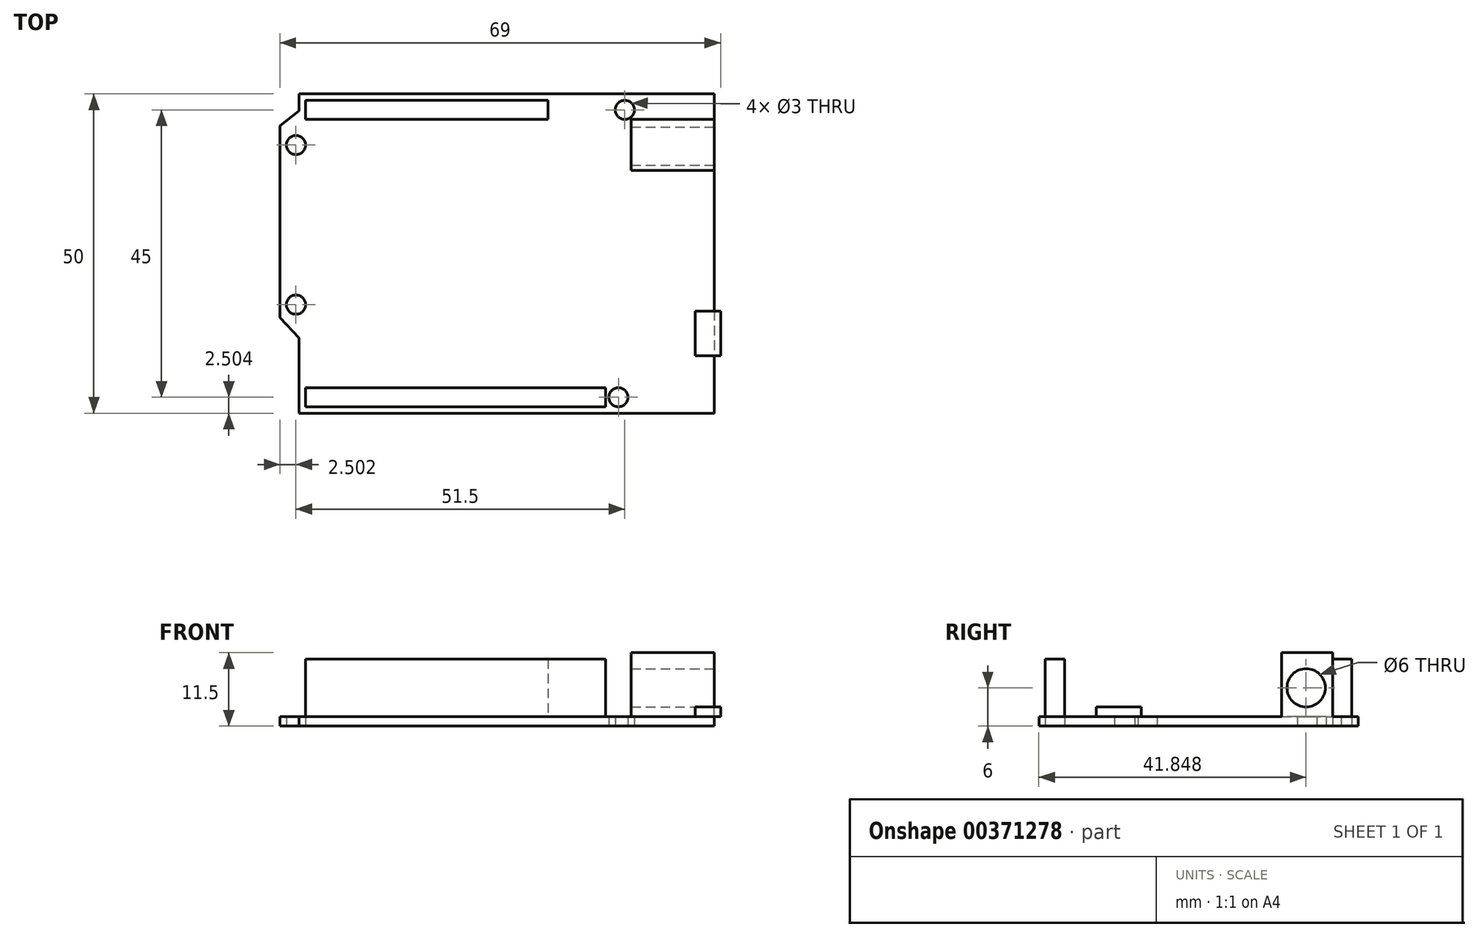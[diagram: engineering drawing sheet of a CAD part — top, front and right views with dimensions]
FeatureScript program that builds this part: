
annotation { "Feature Type Name" : "Feature", "Feature Type Description" : "" }
export const myFeature = defineFeature(function(context is Context, id is Id, definition is map)
    precondition{}
    {
        {
            var Q0;
            Q0=qCreatedBy(makeId("Top.planeOp"),FACE);
            var sketch = newSketch(context, id + "F0", { "sketchPlane" : qUnion([Q0])});
            skLineSegment(sketch, "E0.bottom", {"start": v(15.1, 26.04) * mm, "end": v(-49.9, 26.04) * mm});
            skLineSegment(sketch, "E0.top", {"start": v(15.1, -23.96) * mm, "end": v(-49.9, -23.96) * mm});
            skLineSegment(sketch, "E0.left", {"start": v(15.1, 26.04) * mm, "end": v(15.1, -23.96) * mm});
            skLineSegment(sketch, "E0.right", {"start": v(-49.9, 26.04) * mm, "end": v(-49.9, 23.4) * mm});
            skLineSegment(sketch, "E1", {"start": v(-52.9, 21.04) * mm, "end": v(-52.9, -8.96) * mm});
            skLineSegment(sketch, "E2", {"start": v(-52.9, -8.96) * mm, "end": v(-49.9, -12.14) * mm});
            skLineSegment(sketch, "E3", {"start": v(-52.9, 21.04) * mm, "end": v(-49.9, 23.4) * mm});
            skLineSegment(sketch, "E4.trimOffspring", {"start": v(-49.9, -12.14) * mm, "end": v(-49.9, -23.96) * mm});
            skCircle(sketch, "E5", {"center": v(1.1, 23.54) * mm, "radius": 1.5 * mm});
            skCircle(sketch, "E6", {"center": v(-50.4, 18.04) * mm, "radius": 1.5 * mm});
            skCircle(sketch, "E7", {"center": v(-50.4, -6.96) * mm, "radius": 1.5 * mm});
            skCircle(sketch, "E8", {"center": v(0.1, -21.46) * mm, "radius": 1.5 * mm});
            skSolve(sketch);
        }
        {
            var Q0;
            Q0=makeQuery(id+"F0.imprint","IMPRINT",FACE,{"disambiguationData":[TD([[makeQuery(id+"F0.imprint","IMPRINT",EDGE,{"derivedFrom":sQuery(id+"F0.wireOp",EDGE,"E0.bottom")}),1.0]])]});
            extrude(context, id + "F1", {"entities" : qUnion([Q0]), "depth" : 1.5 * mm});
        }
        {
            var Q0;
            Q0=makeQuery(id+"F1.opExtrude","CAP_FACE",FACE,{"disambiguationData":[OSD([sQuery(id+"F0.wireOp",EDGE,"E0.bottom"),sQuery(id+"F0.wireOp",EDGE,"E0.top"),sQuery(id+"F0.wireOp",EDGE,"E0.left"),sQuery(id+"F0.wireOp",EDGE,"E0.right"),sQuery(id+"F0.wireOp",EDGE,"E1"),sQuery(id+"F0.wireOp",EDGE,"E2"),sQuery(id+"F0.wireOp",EDGE,"E3"),sQuery(id+"F0.wireOp",EDGE,"E4.trimOffspring"),sQuery(id+"F0.wireOp",EDGE,"E5"),sQuery(id+"F0.wireOp",EDGE,"E6"),sQuery(id+"F0.wireOp",EDGE,"E7"),sQuery(id+"F0.wireOp",EDGE,"E8")])],"isStart":false});
            var sketch = newSketch(context, id + "F2", { "sketchPlane" : qUnion([Q0])});
            skLineSegment(sketch, "E9.bottom", {"start": v(-48.9, -19.96) * mm, "end": v(-1.9, -19.96) * mm});
            skLineSegment(sketch, "E9.top", {"start": v(-48.9, -22.96) * mm, "end": v(-1.9, -22.96) * mm});
            skLineSegment(sketch, "E9.left", {"start": v(-48.9, -19.96) * mm, "end": v(-48.9, -22.96) * mm});
            skLineSegment(sketch, "E9.right", {"start": v(-1.9, -19.96) * mm, "end": v(-1.9, -22.96) * mm});
            skLineSegment(sketch, "E10.bottom", {"start": v(-48.9, 22.04) * mm, "end": v(-10.9, 22.04) * mm});
            skLineSegment(sketch, "E10.top", {"start": v(-48.9, 25.04) * mm, "end": v(-10.9, 25.04) * mm});
            skLineSegment(sketch, "E10.left", {"start": v(-48.9, 22.04) * mm, "end": v(-48.9, 25.04) * mm});
            skLineSegment(sketch, "E10.right", {"start": v(-10.9, 22.04) * mm, "end": v(-10.9, 25.04) * mm});
            skLineSegment(sketch, "E11.bottom", {"start": v(17.1, 22.04) * mm, "end": v(4.1, 22.04) * mm});
            skLineSegment(sketch, "E11.top", {"start": v(17.1, 14.04) * mm, "end": v(4.1, 14.04) * mm});
            skLineSegment(sketch, "E11.left", {"start": v(17.1, 22.04) * mm, "end": v(17.1, 14.04) * mm});
            skLineSegment(sketch, "E11.right", {"start": v(4.1, 22.04) * mm, "end": v(4.1, 14.04) * mm});
            skLineSegment(sketch, "E12.bottom", {"start": v(16.1, -4.96) * mm, "end": v(12.1, -4.96) * mm});
            skLineSegment(sketch, "E12.top", {"start": v(16.1, -11.96) * mm, "end": v(12.1, -11.96) * mm});
            skLineSegment(sketch, "E12.left", {"start": v(16.1, -4.96) * mm, "end": v(16.1, -11.96) * mm});
            skLineSegment(sketch, "E12.right", {"start": v(12.1, -4.96) * mm, "end": v(12.1, -11.96) * mm});
            skSolve(sketch);
        }
        {
            var Q0;
            Q0=makeQuery(id+"F2.imprint","IMPRINT",FACE,{"disambiguationData":[TD([[makeQuery(id+"F2.imprint","IMPRINT",EDGE,{"derivedFrom":sQuery(id+"F2.wireOp",EDGE,"E10.bottom")}),1.0]])]});
            var Q1;
            Q1=makeQuery(id+"F2.imprint","IMPRINT",FACE,{"disambiguationData":[TD([[makeQuery(id+"F2.imprint","IMPRINT",EDGE,{"derivedFrom":sQuery(id+"F2.wireOp",EDGE,"E9.bottom")}),-1.0]])]});
            extrude(context, id + "F3", {"entities" : qUnion([Q0, Q1]), "operationType" : NewBodyOperationType.ADD, "depth" : 9 * mm});
        }
        {
            var Q0;
            Q0=makeQuery(id+"F1.opExtrude","CAP_FACE",FACE,{"disambiguationData":[OSD([sQuery(id+"F0.wireOp",EDGE,"E0.bottom"),sQuery(id+"F0.wireOp",EDGE,"E0.top"),sQuery(id+"F0.wireOp",EDGE,"E0.left"),sQuery(id+"F0.wireOp",EDGE,"E0.right"),sQuery(id+"F0.wireOp",EDGE,"E1"),sQuery(id+"F0.wireOp",EDGE,"E2"),sQuery(id+"F0.wireOp",EDGE,"E3"),sQuery(id+"F0.wireOp",EDGE,"E4.trimOffspring"),sQuery(id+"F0.wireOp",EDGE,"E5"),sQuery(id+"F0.wireOp",EDGE,"E6"),sQuery(id+"F0.wireOp",EDGE,"E7"),sQuery(id+"F0.wireOp",EDGE,"E8")])],"isStart":false});
            var sketch = newSketch(context, id + "F4", { "sketchPlane" : qUnion([Q0])});
            skLineSegment(sketch, "E13.bottom", {"start": v(16.1, -7.96) * mm, "end": v(12.1, -7.96) * mm});
            skLineSegment(sketch, "E13.top", {"start": v(16.1, -14.96) * mm, "end": v(12.1, -14.96) * mm});
            skLineSegment(sketch, "E13.left", {"start": v(16.1, -7.96) * mm, "end": v(16.1, -14.96) * mm});
            skLineSegment(sketch, "E13.right", {"start": v(12.1, -7.96) * mm, "end": v(12.1, -14.96) * mm});
            skSolve(sketch);
        }
        {
            var Q0;
            Q0 = qSketchRegion(id + "F4", true);
            extrude(context, id + "F5", {"entities" : qUnion([Q0]), "operationType" : NewBodyOperationType.ADD, "depth" : 1.5 * mm});
        }
        {
            var Q0;
            Q0=makeQuery(id+"F1.opExtrude","SWEPT_FACE",FACE,{"disambiguationData":[OSD([sQuery(id+"F0.wireOp",EDGE,"E0.left")])]});
            var sketch = newSketch(context, id + "F6", { "sketchPlane" : qUnion([Q0])});
            skLineSegment(sketch, "E14.bottom", {"start": v(22.04, 0) * mm, "end": v(14.04, 0) * mm});
            skLineSegment(sketch, "E14.top", {"start": v(22.04, 11.5) * mm, "end": v(14.04, 11.5) * mm});
            skLineSegment(sketch, "E14.left", {"start": v(22.04, 0) * mm, "end": v(22.04, 11.5) * mm});
            skLineSegment(sketch, "E14.right", {"start": v(14.04, 0) * mm, "end": v(14.04, 11.5) * mm});
            skCircle(sketch, "E15", {"center": v(17.89, 6) * mm, "radius": 3 * mm});
            skSolve(sketch);
        }
        {
            var Q0;
            {var subQ0=sQuery(id+"F6.wireOp",EDGE,"E14.bottom");Q0=makeQuery(id+"F6.imprint","IMPRINT",FACE,{"disambiguationData":[TD([[makeQuery(id+"F6.imprint","IMPRINT",EDGE,{"derivedFrom":subQ0}),-1.0]])]});}
            var Q1;
            {var subQ1=sQuery(id+"F6.wireOp",EDGE,"E14.top");Q1=makeQuery(id+"F6.imprint","IMPRINT",FACE,{"disambiguationData":[TD([[makeQuery(id+"F6.imprint","IMPRINT",EDGE,{"derivedFrom":subQ1}),1.0]])]});}
            extrude(context, id + "F7", {"entities" : qUnion([Q0, Q1]), "operationType" : NewBodyOperationType.ADD, "oppositeDirection" : true, "depth" : 13 * mm});
        }
    });
